# Revit family: VIESSMANN - Vitocrossal 100 CIB
name_source: partatom
category: Wyposażenie mechaniczne
revit_build: Autodesk Revit 2017 (Build: 20160720_1515(x64)
units: mm (PartAtom-declared; Revit-internal decimal feet)

## family parameters
Numer OmniClass = 23.15.30.27.21
Oparty na płaszczyźnie roboczej = Nie
Punkt obliczania pomieszczeń = Nie
Tnij formami wycięć po wczytaniu = Tak
Typ części = Normalny
Tytuł OmniClass = Gas Tanks and Gasholders
Współdzielony = Nie
Wymiar okrągłego złącza = Użyj średnicy
Zawsze pionowo = Tak

## types (8) — shared parameters
Autor = www.archispace.pl
Ciśnienie kontrolne = 0.8 MPa
Ciśnienie na przyłączu gazu E/GZ50/G20 oraz Lw/GZ41,5/G27 = 2/2.5 kPa
Częstotliwość = 50 Hz
Dop. maks. ciśnienie robocze = 0.6 MPa
Dop. min. ciśnienie robocze = 0.1 MPa
Dop. temperatura na zasilaniu (=temperatura progowa) = 110 °C
Dop. temperatura robocza = 95 °C
Liczba biegunów = 1
NOx = Klasa 6, <56 mg/kWh
Napięcie zasilania = 230 V
Numer identyfikacyjny produktu = CE-0085CR0391
Odpływ kondensatu = 12.70 mm
Odsunięcie RLU = 90 mm  [stored 0.295276 ft]
Odsunięcie powrotu do kotła od osi = 190 mm
Odsunięcie spustu = 107 mm  [stored 0.35105 ft]
Opis = Gazowy kocioł grzewczy
Opis indeksowy = CE-0085CR0391
Opory przepływu = 0.0 MPa
Parametry produktu wg. EnEV - sprawność znormalizowana przy temperaturze w systemie grzewczym wyn. 40/30°C = do 98 (Hs)/109 (Hi)
Parametry produktu wg. EnEV - sprawność znormalizowana przy temperaturze w systemie grzewczym wyn. 75/60°C = do 96 (Hs)/106 (Hi)
Parametry spalin - dyspozycyjne ciśnienie tłoczenia na króćcu spalin = 0.0 MPa
Parametry spalin - przy obciążeniu częściowym (przy temp. wody na powrocie wyn. 30°C) = 35 °C
Parametry spalin - przy znamionowej mocy cieplnej (przy temp. wody na powrocie wyn. 30°C) = 45 °C
Parametry spalin - temperatura (przy temp. wody na powrocie wyn. 60°C) = 65 °C
Producent = Viessmann Sp.z.o.o.
Przyłącze powietrza do spalania z zewnątrz (opcja dodatkowa) = 80 mm  [stored 0.262467 ft]
Przyłącze spalin = 200 mm  [stored 0.656168 ft]
Przyłącze zabezpieczające (zawór bezpieczeństwa) = 1 1/4"
Spust = 1 1/4"
Szerokość = 750 mm  [stored 2.46063 ft]
Szerokość fundamentu = 800 mm
Szerokość palnika = 463 mm  [stored 1.51903 ft]
Szerokość podstawy = 680 mm  [stored 2.23097 ft]
URL = https://www.viessmann-projektant.pl
Viessmann Kolor 1 = Viessmann Kolor 1
Viessmann Kolor 2 = Viessmann Kolor 2
Viessmann Kolor 3 = Viessmann Kolor 3
Współczynnik mocy = 1
Wykonanie palnika = Wbudowany modulowany
Wysokość = 1450 mm
Wysokość fundamentu = 100 mm  [stored 0.328084 ft]
Wysokość króćca zasialania z kotła = 1650 mm
Wysokość króćca zaworu bezp. = 1530 mm

## per-type parameters (varying)
- CIB 80kW: Długość=1027 mm; Długość całkowita do króćca powrotu=739 mm  [stored 2.42454 ft]; Długość fundamentu=750 mm  [stored 2.46063 ft]; Długość korpusu=683 mm  [stored 2.24081 ft]; Długość palnika=442 mm  [stored 1.45013 ft]; Masa - całkowita masa jednostki=238.00 kg; Masa - jednostka w opakowaniu=288.00 kg; Masa - korpus kotła=183.00 kg; Masa - korpus kotła z paletą transportową=210.00 kg; Masa - palnik=10.00 kg; Moc cieplna palnika dolna=76 kW; Moc cieplna palnika górna=15 kW; Moc nominalna=80 kW; Model=Gazowy kocioł kondensacyjny Viessmann Vitocrossal CIB 80kW / Gas condensing boiler Viessmann Vitocrossal CIB 80kW; Odległość do króćca powrotu=655 mm  [stored 2.14895 ft]; Odsunięcie króćca zasialania z kotła=492 mm  [stored 1.61417 ft]; Odsunięcie osi przyłącza spalin=243 mm; PN 6 DN - powrót do kotła=50 mm  [stored 0.164042 ft]; PN 6 DN - zasilanie z kotła=50 mm  [stored 0.164042 ft]; Parametry spalin - masowe natężenie przepływu w przypadku gazu ziemnego przy obciążeniu częściowym=36 kg/h; Parametry spalin - masowe natężenie przepływu w przypadku gazu ziemnego przy znamionowej mocy cieplnej=120 kg/h; Pobór mocy elektrycznej - przy dolnej mocy cieplnej=20 W; Pobór mocy elektrycznej - przy górnej mocy cieplnej=141 W; Pojemność wodna kotła=65.0 L; Przepływ maksymalny=1.0 L/s; Przyłącze gazu=1"; Straty energii dyżurnej qB,70=0.6%; Typ palnika=CI 75/80 kW; Wartości przyłączeniowe (w odniesieniu do maks. obciążenia) gazem ziemnym E/GZ50/G20 - obciążenie częściowe=0.4 L/s; Wartości przyłączeniowe (w odniesieniu do maks. obciążenia) gazem ziemnym E/GZ50/G20 - obciążenie pełne=2.2 L/s; Wartości przyłączeniowe (w odniesieniu do maks. obciążenia) gazem ziemnym Lw/GZ41,5/G27 - obciążenie częściowe=0.5 L/s; Wartości przyłączeniowe (w odniesieniu do maks. obciążenia) gazem ziemnym Lw/GZ41,5/G27 - obciążenie pełne=2.6 L/s; Wysokość RLU=126 mm  [stored 0.413386 ft]; Wysokość króćca powrotu do kotła=195 mm  [stored 0.639764 ft]; Wysokość króćca spalin=800 mm; Wysokość palnika=400 mm  [stored 1.31234 ft]; Wysokość spustu=337 mm  [stored 1.10564 ft]; Zakres znamionowej mocy cieplnej przy Tv/Tr 50/30°C=16 - 80; Zakres znamionowej mocy cieplnej przy Tv/Tr 80/60°C=15 - 74; Znamionowe obciążenie cieplne=76 kW
- CIB 120kW: Długość=1154 mm; Długość całkowita do króćca powrotu=862 mm; Długość fundamentu=1200 mm; Długość korpusu=810 mm; Długość palnika=481 mm  [stored 1.57808 ft]; Masa - całkowita masa jednostki=295.00 kg; Masa - jednostka w opakowaniu=345.00 kg; Masa - korpus kotła=230.00 kg; Masa - korpus kotła z paletą transportową=260.00 kg; Masa - palnik=11.00 kg; Moc cieplna palnika dolna=113 kW; Moc cieplna palnika górna=30 kW; Moc nominalna=120 kW; Model=Gazowy kocioł kondensacyjny Viessmann Vitocrossal CIB 120kW / Gas condensing boiler Viessmann Vitocrossal CIB 120kW; Odległość do króćca powrotu=770 mm  [stored 2.52625 ft]; Odsunięcie króćca zasialania z kotła=500 mm  [stored 1.64042 ft]; Odsunięcie osi przyłącza spalin=243 mm; PN 6 DN - powrót do kotła=50 mm  [stored 0.164042 ft]; PN 6 DN - zasilanie z kotła=50 mm  [stored 0.164042 ft]; Parametry spalin - masowe natężenie przepływu w przypadku gazu ziemnego przy obciążeniu częściowym=54 kg/h; Parametry spalin - masowe natężenie przepływu w przypadku gazu ziemnego przy znamionowej mocy cieplnej=180 kg/h; Pobór mocy elektrycznej - przy dolnej mocy cieplnej=28 W; Pobór mocy elektrycznej - przy górnej mocy cieplnej=130 W; Pojemność wodna kotła=103.0 L; Przepływ maksymalny=1.4 L/s; Przyłącze gazu=1 1/2"; Straty energii dyżurnej qB,70=0.5%; Typ palnika=CI 120/160 kW; Wartości przyłączeniowe (w odniesieniu do maks. obciążenia) gazem ziemnym E/GZ50/G20 - obciążenie częściowe=0.9 L/s; Wartości przyłączeniowe (w odniesieniu do maks. obciążenia) gazem ziemnym E/GZ50/G20 - obciążenie pełne=3.3 L/s; Wartości przyłączeniowe (w odniesieniu do maks. obciążenia) gazem ziemnym Lw/GZ41,5/G27 - obciążenie częściowe=1.0 L/s; Wartości przyłączeniowe (w odniesieniu do maks. obciążenia) gazem ziemnym Lw/GZ41,5/G27 - obciążenie pełne=3.9 L/s; Wysokość RLU=126 mm  [stored 0.413386 ft]; Wysokość króćca powrotu do kotła=189 mm  [stored 0.620079 ft]; Wysokość króćca spalin=794 mm; Wysokość palnika=273 mm  [stored 0.895669 ft]; Wysokość spustu=331 mm  [stored 1.08596 ft]; Zakres znamionowej mocy cieplnej przy Tv/Tr 50/30°C=32 - 120; Zakres znamionowej mocy cieplnej przy Tv/Tr 80/60°C=29 - 110; Znamionowe obciążenie cieplne=113 kW
- CIB 160kW: Długość=1154 mm; Długość całkowita do króćca powrotu=862 mm; Długość fundamentu=1200 mm; Długość korpusu=810 mm; Długość palnika=481 mm  [stored 1.57808 ft]; Masa - całkowita masa jednostki=295.00 kg; Masa - jednostka w opakowaniu=345.00 kg; Masa - korpus kotła=230.00 kg; Masa - korpus kotła z paletą transportową=260.00 kg; Masa - palnik=11.00 kg; Moc cieplna palnika dolna=151 kW; Moc cieplna palnika górna=30 kW; Moc nominalna=160 kW; Model=Gazowy kocioł kondensacyjny Viessmann Vitocrossal CIB 160kW / Gas condensing boiler Viessmann Vitocrossal CIB 160kW; Odległość do króćca powrotu=770 mm  [stored 2.52625 ft]; Odsunięcie króćca zasialania z kotła=500 mm  [stored 1.64042 ft]; Odsunięcie osi przyłącza spalin=243 mm; PN 6 DN - powrót do kotła=50 mm  [stored 0.164042 ft]; PN 6 DN - zasilanie z kotła=50 mm  [stored 0.164042 ft]; Parametry spalin - masowe natężenie przepływu w przypadku gazu ziemnego przy obciążeniu częściowym=72 kg/h; Parametry spalin - masowe natężenie przepływu w przypadku gazu ziemnego przy znamionowej mocy cieplnej=240 kg/h; Pobór mocy elektrycznej - przy dolnej mocy cieplnej=28 W; Pobór mocy elektrycznej - przy górnej mocy cieplnej=268 W; Pojemność wodna kotła=103.0 L; Przepływ maksymalny=1.9 L/s; Przyłącze gazu=1 1/2"; Straty energii dyżurnej qB,70=0.3%; Typ palnika=CI 120/160 kW; Wartości przyłączeniowe (w odniesieniu do maks. obciążenia) gazem ziemnym E/GZ50/G20 - obciążenie częściowe=0.9 L/s; Wartości przyłączeniowe (w odniesieniu do maks. obciążenia) gazem ziemnym E/GZ50/G20 - obciążenie pełne=4.4 L/s; Wartości przyłączeniowe (w odniesieniu do maks. obciążenia) gazem ziemnym Lw/GZ41,5/G27 - obciążenie częściowe=1.0 L/s; Wartości przyłączeniowe (w odniesieniu do maks. obciążenia) gazem ziemnym Lw/GZ41,5/G27 - obciążenie pełne=5.2 L/s; Wysokość RLU=126 mm  [stored 0.413386 ft]; Wysokość króćca powrotu do kotła=189 mm  [stored 0.620079 ft]; Wysokość króćca spalin=794 mm; Wysokość palnika=273 mm  [stored 0.895669 ft]; Wysokość spustu=331 mm  [stored 1.08596 ft]; Zakres znamionowej mocy cieplnej przy Tv/Tr 50/30°C=32 - 160; Zakres znamionowej mocy cieplnej przy Tv/Tr 80/60°C=29 - 146; Znamionowe obciążenie cieplne=151 kW
- CIB 75kW: Długość=1027 mm; Długość całkowita do króćca powrotu=739 mm  [stored 2.42454 ft]; Długość fundamentu=750 mm  [stored 2.46063 ft]; Długość korpusu=683 mm  [stored 2.24081 ft]; Długość palnika=442 mm  [stored 1.45013 ft]; Masa - całkowita masa jednostki=238.00 kg; Masa - jednostka w opakowaniu=288.00 kg; Masa - korpus kotła=183.00 kg; Masa - korpus kotła z paletą transportową=210.00 kg; Masa - palnik=10.00 kg; Moc cieplna palnika dolna=71 kW; Moc cieplna palnika górna=15 kW; Moc nominalna=75 kW; Model=Gazowy kocioł kondensacyjny Viessmann Vitocrossal CIB 75kW / Gas condensing boiler Viessmann Vitocrossal CIB 75kW; Odległość do króćca powrotu=655 mm  [stored 2.14895 ft]; Odsunięcie króćca zasialania z kotła=492 mm  [stored 1.61417 ft]; Odsunięcie osi przyłącza spalin=243 mm; PN 6 DN - powrót do kotła=50 mm  [stored 0.164042 ft]; PN 6 DN - zasilanie z kotła=50 mm  [stored 0.164042 ft]; Parametry spalin - masowe natężenie przepływu w przypadku gazu ziemnego przy obciążeniu częściowym=34 kg/h; Parametry spalin - masowe natężenie przepływu w przypadku gazu ziemnego przy znamionowej mocy cieplnej=112 kg/h; Pobór mocy elektrycznej - przy dolnej mocy cieplnej=20 W; Pobór mocy elektrycznej - przy górnej mocy cieplnej=121 W; Pojemność wodna kotła=65.0 L; Przepływ maksymalny=0.9 L/s; Przyłącze gazu=1"; Straty energii dyżurnej qB,70=0.7 %; Typ palnika=CI 75/80 kW; Wartości przyłączeniowe (w odniesieniu do maks. obciążenia) gazem ziemnym E/GZ50/G20 - obciążenie częściowe=0.4 L/s; Wartości przyłączeniowe (w odniesieniu do maks. obciążenia) gazem ziemnym E/GZ50/G20 - obciążenie pełne=2.1 L/s; Wartości przyłączeniowe (w odniesieniu do maks. obciążenia) gazem ziemnym Lw/GZ41,5/G27 - obciążenie częściowe=0.5 L/s; Wartości przyłączeniowe (w odniesieniu do maks. obciążenia) gazem ziemnym Lw/GZ41,5/G27 - obciążenie pełne=2.4 L/s; Wysokość RLU=126 mm  [stored 0.413386 ft]; Wysokość króćca powrotu do kotła=195 mm  [stored 0.639764 ft]; Wysokość króćca spalin=800 mm; Wysokość palnika=400 mm  [stored 1.31234 ft]; Wysokość spustu=337 mm  [stored 1.10564 ft]; Zakres znamionowej mocy cieplnej przy Tv/Tr 50/30°C=16 - 75; Zakres znamionowej mocy cieplnej przy Tv/Tr 80/60°C=15 - 69; Znamionowe obciążenie cieplne=71 kW
- CIB 200kW: Długość=1256 mm; Długość całkowita do króćca powrotu=967 mm; Długość fundamentu=1650 mm; Długość korpusu=904 mm; Długość palnika=655 mm  [stored 2.14895 ft]; Masa - całkowita masa jednostki=340.00 kg; Masa - jednostka w opakowaniu=390.00 kg; Masa - korpus kotła=265.00 kg; Masa - korpus kotła z paletą transportową=295.00 kg; Masa - palnik=15.00 kg; Moc cieplna palnika dolna=189 kW; Moc cieplna palnika górna=45 kW; Moc nominalna=200 kW; Model=Gazowy kocioł kondensacyjny Viessmann Vitocrossal CIB 200kW / Gas condensing boiler Viessmann Vitocrossal CIB 200kW; Odległość do króćca powrotu=890 mm; Odsunięcie króćca zasialania z kotła=492 mm  [stored 1.61417 ft]; Odsunięcie osi przyłącza spalin=248 mm  [stored 0.813648 ft]; PN 6 DN - powrót do kotła=65 mm  [stored 0.213255 ft]; PN 6 DN - zasilanie z kotła=65 mm  [stored 0.213255 ft]; Parametry spalin - masowe natężenie przepływu w przypadku gazu ziemnego przy obciążeniu częściowym=90 kg/h; Parametry spalin - masowe natężenie przepływu w przypadku gazu ziemnego przy znamionowej mocy cieplnej=300 kg/h; Pobór mocy elektrycznej - przy dolnej mocy cieplnej=29 W; Pobór mocy elektrycznej - przy górnej mocy cieplnej=171 W; Pojemność wodna kotła=145.0 L; Przepływ maksymalny=2.4 L/s; Przyłącze gazu=1 1/2"; Straty energii dyżurnej qB,70=0.6%; Typ palnika=CI 200/240 kW; Wartości przyłączeniowe (w odniesieniu do maks. obciążenia) gazem ziemnym E/GZ50/G20 - obciążenie częściowe=1.3 L/s; Wartości przyłączeniowe (w odniesieniu do maks. obciążenia) gazem ziemnym E/GZ50/G20 - obciążenie pełne=5.6 L/s; Wartości przyłączeniowe (w odniesieniu do maks. obciążenia) gazem ziemnym Lw/GZ41,5/G27 - obciążenie częściowe=1.6 L/s; Wartości przyłączeniowe (w odniesieniu do maks. obciążenia) gazem ziemnym Lw/GZ41,5/G27 - obciążenie pełne=6.5 L/s; Wysokość RLU=146 mm  [stored 0.479003 ft]; Wysokość króćca powrotu do kotła=183 mm  [stored 0.600394 ft]; Wysokość króćca spalin=789 mm; Wysokość palnika=356 mm  [stored 1.16798 ft]; Wysokość spustu=325 mm  [stored 1.06627 ft]; Zakres znamionowej mocy cieplnej przy Tv/Tr 50/30°C=48 - 200; Zakres znamionowej mocy cieplnej przy Tv/Tr 80/60°C=44 - 184; Znamionowe obciążenie cieplne=189 kW
- CIB 240kW: Długość=1256 mm; Długość całkowita do króćca powrotu=967 mm; Długość fundamentu=1650 mm; Długość korpusu=904 mm; Długość palnika=655 mm  [stored 2.14895 ft]; Masa - całkowita masa jednostki=340.00 kg; Masa - jednostka w opakowaniu=390.00 kg; Masa - korpus kotła=265.00 kg; Masa - korpus kotła z paletą transportową=295.00 kg; Masa - palnik=15.00 kg; Moc cieplna palnika dolna=226 kW; Moc cieplna palnika górna=45 kW; Moc nominalna=240 kW; Model=Gazowy kocioł kondensacyjny Viessmann Vitocrossal CIB 240kW / Gas condensing boiler Viessmann Vitocrossal CIB 240kW; Odległość do króćca powrotu=890 mm; Odsunięcie króćca zasialania z kotła=492 mm  [stored 1.61417 ft]; Odsunięcie osi przyłącza spalin=248 mm  [stored 0.813648 ft]; PN 6 DN - powrót do kotła=65 mm  [stored 0.213255 ft]; PN 6 DN - zasilanie z kotła=65 mm  [stored 0.213255 ft]; Parametry spalin - masowe natężenie przepływu w przypadku gazu ziemnego przy obciążeniu częściowym=108 kg/h; Parametry spalin - masowe natężenie przepływu w przypadku gazu ziemnego przy znamionowej mocy cieplnej=360 kg/h; Pobór mocy elektrycznej - przy dolnej mocy cieplnej=29 W; Pobór mocy elektrycznej - przy górnej mocy cieplnej=279 W; Pojemność wodna kotła=145.0 L; Przepływ maksymalny=2.9 L/s; Przyłącze gazu=1 1/2"; Straty energii dyżurnej qB,70=0.6%; Typ palnika=CI 200/240 kW; Wartości przyłączeniowe (w odniesieniu do maks. obciążenia) gazem ziemnym E/GZ50/G20 - obciążenie częściowe=1.3 L/s; Wartości przyłączeniowe (w odniesieniu do maks. obciążenia) gazem ziemnym E/GZ50/G20 - obciążenie pełne=6.5 L/s; Wartości przyłączeniowe (w odniesieniu do maks. obciążenia) gazem ziemnym Lw/GZ41,5/G27 - obciążenie częściowe=1.6 L/s; Wartości przyłączeniowe (w odniesieniu do maks. obciążenia) gazem ziemnym Lw/GZ41,5/G27 - obciążenie pełne=7.7 L/s; Wysokość RLU=146 mm  [stored 0.479003 ft]; Wysokość króćca powrotu do kotła=183 mm  [stored 0.600394 ft]; Wysokość króćca spalin=789 mm; Wysokość palnika=356 mm  [stored 1.16798 ft]; Wysokość spustu=325 mm  [stored 1.06627 ft]; Zakres znamionowej mocy cieplnej przy Tv/Tr 50/30°C=48 - 240; Zakres znamionowej mocy cieplnej przy Tv/Tr 80/60°C=44 - 220; Znamionowe obciążenie cieplne=226 kW
- CIB 280kW: Długość=1375 mm; Długość całkowita do króćca powrotu=1085 mm; Długość fundamentu=1650 mm; Długość korpusu=1021 mm; Długość palnika=731 mm  [stored 2.39829 ft]; Masa - całkowita masa jednostki=385.00 kg; Masa - jednostka w opakowaniu=435.00 kg; Masa - korpus kotła=300.00 kg; Masa - korpus kotła z paletą transportową=330.00 kg; Masa - palnik=15.00 kg; Moc cieplna palnika dolna=264 kW; Moc cieplna palnika górna=60 kW; Moc nominalna=280 kW; Model=Gazowy kocioł kondensacyjny Viessmann Vitocrossal CIB 280kW / Gas condensing boiler Viessmann Vitocrossal CIB 280kW; Odległość do króćca powrotu=1004 mm; Odsunięcie króćca zasialania z kotła=492 mm  [stored 1.61417 ft]; Odsunięcie osi przyłącza spalin=253 mm  [stored 0.830052 ft]; PN 6 DN - powrót do kotła=65 mm  [stored 0.213255 ft]; PN 6 DN - zasilanie z kotła=65 mm  [stored 0.213255 ft]; Parametry spalin - masowe natężenie przepływu w przypadku gazu ziemnego przy obciążeniu częściowym=126 kg/h; Parametry spalin - masowe natężenie przepływu w przypadku gazu ziemnego przy znamionowej mocy cieplnej=420 kg/h; Pobór mocy elektrycznej - przy dolnej mocy cieplnej=27 W; Pobór mocy elektrycznej - przy górnej mocy cieplnej=260 W; Pojemność wodna kotła=180.0 L; Przepływ maksymalny=3.4 L/s; Przyłącze gazu=1 1/2"; Straty energii dyżurnej qB,70=0.6%; Typ palnika=CI 280/318 kW; Wartości przyłączeniowe (w odniesieniu do maks. obciążenia) gazem ziemnym E/GZ50/G20 - obciążenie częściowe=1.8 L/s; Wartości przyłączeniowe (w odniesieniu do maks. obciążenia) gazem ziemnym E/GZ50/G20 - obciążenie pełne=7.8 L/s; Wartości przyłączeniowe (w odniesieniu do maks. obciążenia) gazem ziemnym Lw/GZ41,5/G27 - obciążenie częściowe=2.1 L/s; Wartości przyłączeniowe (w odniesieniu do maks. obciążenia) gazem ziemnym Lw/GZ41,5/G27 - obciążenie pełne=9.0 L/s; Wysokość RLU=136 mm; Wysokość króćca powrotu do kotła=177 mm  [stored 0.580709 ft]; Wysokość króćca spalin=783 mm  [stored 2.5689 ft]; Wysokość palnika=356 mm  [stored 1.16798 ft]; Wysokość spustu=319 mm  [stored 1.04659 ft]; Zakres znamionowej mocy cieplnej przy Tv/Tr 50/30°C=64 - 280; Zakres znamionowej mocy cieplnej przy Tv/Tr 80/60°C=58 - 258; Znamionowe obciążenie cieplne=264 kW
- CIB 318kW: Długość=1375 mm; Długość całkowita do króćca powrotu=1085 mm; Długość fundamentu=1650 mm; Długość korpusu=1021 mm; Długość palnika=393 mm  [stored 1.28937 ft]; Masa - całkowita masa jednostki=385.00 kg; Masa - jednostka w opakowaniu=435.00 kg; Masa - korpus kotła=300.00 kg; Masa - korpus kotła z paletą transportową=330.00 kg; Masa - palnik=15.00 kg; Moc cieplna palnika dolna=300 kW; Moc cieplna palnika górna=60 kW; Moc nominalna=318 kW; Model=Gazowy kocioł kondensacyjny Viessmann Vitocrossal CIB 318kW / Gas condensing boiler Viessmann Vitocrossal CIB 318kW; Odległość do króćca powrotu=1004 mm; Odsunięcie króćca zasialania z kotła=492 mm  [stored 1.61417 ft]; Odsunięcie osi przyłącza spalin=253 mm  [stored 0.830052 ft]; PN 6 DN - powrót do kotła=65 mm  [stored 0.213255 ft]; PN 6 DN - zasilanie z kotła=65 mm  [stored 0.213255 ft]; Parametry spalin - masowe natężenie przepływu w przypadku gazu ziemnego przy obciążeniu częściowym=143 kg/h; Parametry spalin - masowe natężenie przepływu w przypadku gazu ziemnego przy znamionowej mocy cieplnej=477 kg/h; Pobór mocy elektrycznej - przy dolnej mocy cieplnej=27 W; Pobór mocy elektrycznej - przy górnej mocy cieplnej=393 W; Pojemność wodna kotła=180.0 L; Przepływ maksymalny=3.8 L/s; Przyłącze gazu=1 1/2"; Straty energii dyżurnej qB,70=0.6%; Typ palnika=CI 280/318 kW; Wartości przyłączeniowe (w odniesieniu do maks. obciążenia) gazem ziemnym E/GZ50/G20 - obciążenie częściowe=1.8 L/s; Wartości przyłączeniowe (w odniesieniu do maks. obciążenia) gazem ziemnym E/GZ50/G20 - obciążenie pełne=8.8 L/s; Wartości przyłączeniowe (w odniesieniu do maks. obciążenia) gazem ziemnym Lw/GZ41,5/G27 - obciążenie częściowe=2.1 L/s; Wartości przyłączeniowe (w odniesieniu do maks. obciążenia) gazem ziemnym Lw/GZ41,5/G27 - obciążenie pełne=10.3 L/s; Wysokość RLU=136 mm; Wysokość króćca powrotu do kotła=177 mm  [stored 0.580709 ft]; Wysokość króćca spalin=783 mm  [stored 2.5689 ft]; Wysokość palnika=27 mm; Wysokość spustu=319 mm  [stored 1.04659 ft]; Zakres znamionowej mocy cieplnej przy Tv/Tr 50/30°C=64 - 318; Zakres znamionowej mocy cieplnej przy Tv/Tr 80/60°C=58 - 291; Znamionowe obciążenie cieplne=300 kW

note: [stored X ft] marks values corroborated as IEEE doubles in the binary element streams (Revit-internal decimal feet)
